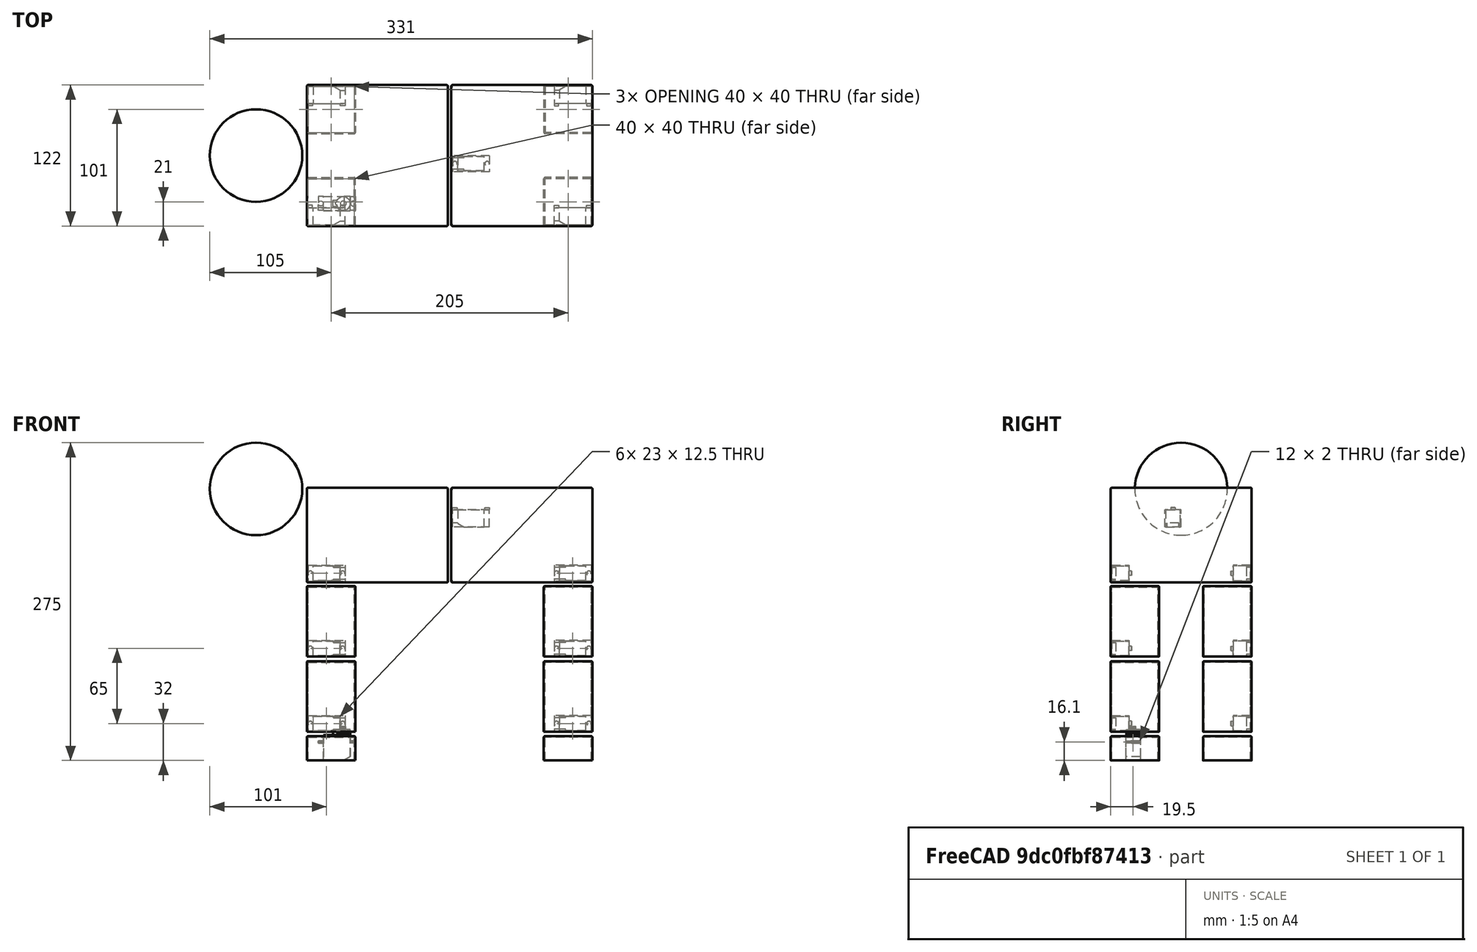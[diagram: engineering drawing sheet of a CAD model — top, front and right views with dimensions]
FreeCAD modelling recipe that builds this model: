
FCSTD DOCUMENT  (FreeCAD 0.21R33771 (Git))
Label: draft 1
License: All rights reserved
LicenseURL: https://en.wikipedia.org/wiki/All_rights_reserved
objects: Part::Box×42, Part::Cylinder×28, Part::Cut×28, Part::MultiFuse×18, Part::Feature×15, Part::Thickness×14, Part::Mirroring×3, Part::Sphere×1
note: 149 computed .brp shape members not serialized (recipe doc carries the construction recipe); baked Part::Feature solids carry a one-line shape summary decoded from their .brp

FEATURE [Part::Box] Box  label="leg down"
  AttacherType = Attacher::AttachEngine3D
  Height = 60
  Length = 40
  Placement = pos=(0,0,25) rot=(0,0,1;0rad)
  Width = 40
FEATURE [Part::Feature] _g_servo002_solid  label="9g_servo"
  Placement = pos=(25,18.5,11.1) rot=(0,0,1;0rad)
  shape: bbox 32 x 12.5 x 29.27 mm, 117 faces (baked)
FEATURE [Part::Box] Box001  label="paw"
  AttacherType = Attacher::AttachEngine3D
  Height = 20
  Length = 40
  Width = 40
FEATURE [Part::Box] Box003  label="Cube"
  AttacherType = Attacher::AttachEngine3D
  Height = 80
  Length = 120
  Placement = pos=(0,0,155) rot=(0,0,1;0rad)
  Width = 120
FEATURE [Part::Box] Box004  label="Cube001"
  AttacherType = Attacher::AttachEngine3D
  Height = 80
  Length = 120
  Placement = pos=(125,0,155) rot=(0,0,1;0rad)
  Width = 120
FEATURE [Part::Sphere] Sphere  label="Head"
  Angle1 = -90
  Angle2 = 90
  Angle3 = 360
  AttacherType = Attacher::AttachEngine3D
  Placement = pos=(-45,60,235) rot=(0,0,1;0rad)
  Radius = 40
FEATURE [Part::Box] Box015  label="Cube003"
  AttacherType = Attacher::AttachEngine3D
  Height = 14.9
  Length = 32
  Width = 14
FEATURE [Part::Box] Box016  label="Cube004"
  AttacherType = Attacher::AttachEngine3D
  Height = 3.5
  Length = 10
  Placement = pos=(22,2,0) rot=(0,0,1;0rad)
  Width = 10
FEATURE [Part::Cylinder] Cylinder002  label="Cylindre002"
  Angle = 360
  AttacherType = Attacher::AttachEngine3D
  FirstAngle = 0
  Height = 2.1
  Placement = pos=(2,7,14.9) rot=(0,0,1;0rad)
  Radius = 1.95
  SecondAngle = 0
FEATURE [Part::Cylinder] Cylinder003  label="Cylindre003"
  Angle = 360
  AttacherType = Attacher::AttachEngine3D
  FirstAngle = 0
  Height = 2.1
  Placement = pos=(30,7,14.9) rot=(0,0,1;0rad)
  Radius = 1.95
  SecondAngle = 0
FEATURE [Part::Feature] _g_servo002_solid002  label="9g_servo002"
  Placement = pos=(16,7,11) rot=(0,0,1;0rad)
  shape: bbox 32 x 12.5 x 29.27 mm, 117 faces (baked)
FEATURE [Part::Cut] Cut001
  Base = -> Box015
  Tool = -> _g_servo002_solid002
FEATURE [Part::MultiFuse] Fusion007
  Shapes = -> [Cut001,Cylinder002,Cylinder003]
FEATURE [Part::Cut] Cut002  label="ServoSocket"
  Base = -> Fusion007
  Placement = pos=(0,0,39) rot=(-1,0,0;1.5708rad)
  Tool = -> Box016
FEATURE [Part::Box] Box017  label="Cube005"
  AttacherType = Attacher::AttachEngine3D
  Height = 14.9
  Length = 32
  Width = 14
FEATURE [Part::Box] Box018  label="Cube006"
  AttacherType = Attacher::AttachEngine3D
  Height = 3.5
  Length = 10
  Placement = pos=(22,2,0) rot=(0,0,1;0rad)
  Width = 10
FEATURE [Part::Cylinder] Cylinder004  label="Cylindre004"
  Angle = 360
  AttacherType = Attacher::AttachEngine3D
  FirstAngle = 0
  Height = 2.1
  Placement = pos=(2,7,14.9) rot=(0,0,1;0rad)
  Radius = 1.95
  SecondAngle = 0
FEATURE [Part::Cylinder] Cylinder005  label="Cylindre005"
  Angle = 360
  AttacherType = Attacher::AttachEngine3D
  FirstAngle = 0
  Height = 2.1
  Placement = pos=(30,7,14.9) rot=(0,0,1;0rad)
  Radius = 1.95
  SecondAngle = 0
FEATURE [Part::Feature] _g_servo002_solid003  label="9g_servo003"
  Placement = pos=(16,7,11) rot=(0,0,1;0rad)
  shape: bbox 32 x 12.5 x 29.27 mm, 117 faces (baked)
FEATURE [Part::Cut] Cut003
  Base = -> Box017
  Tool = -> _g_servo002_solid003
FEATURE [Part::MultiFuse] Fusion008
  Shapes = -> [Cut003,Cylinder004,Cylinder005]
FEATURE [Part::Cut] Cut004  label="ServoSocket001"
  Base = -> Fusion008
  Placement = pos=(0,0,39) rot=(-1,0,0;1.5708rad)
  Tool = -> Box018
FEATURE [Part::Thickness] Thickness  label="LegDown"
  Faces = -> Box [Face5]
  Intersection = false
  Join = 0
  Mode = 0
  SelfIntersection = false
  Value = 1
FEATURE [Part::Thickness] Thickness002  label="Paw"
  Faces = -> Box001 [Face5]
  Intersection = false
  Join = 0
  Mode = 0
  SelfIntersection = false
  Value = 1
FEATURE [Part::Thickness] Thickness003  label="BodyFront"
  Faces = -> Box003
  Intersection = false
  Join = 0
  Mode = 0
  SelfIntersection = false
  Value = 1
FEATURE [Part::Thickness] Thickness004  label="BodyBack"
  Faces = -> Box004
  Intersection = false
  Join = 0
  Mode = 0
  SelfIntersection = false
  Value = 1
FEATURE [Part::Box] Box019  label="leg down001"
  AttacherType = Attacher::AttachEngine3D
  Height = 60
  Length = 40
  Placement = pos=(0,0,90) rot=(0,0,1;0rad)
  Width = 40
FEATURE [Part::Thickness] Thickness005  label="LegUp"
  Faces = -> Box019 [Face5]
  Intersection = false
  Join = 0
  Mode = 0
  SelfIntersection = false
  Value = 1
FEATURE [Part::Box] Box020  label="Cube007"
  AttacherType = Attacher::AttachEngine3D
  Height = 14.9
  Length = 32
  Width = 14
FEATURE [Part::Box] Box021  label="Cube008"
  AttacherType = Attacher::AttachEngine3D
  Height = 3.5
  Length = 10
  Placement = pos=(22,2,0) rot=(0,0,1;0rad)
  Width = 10
FEATURE [Part::Cylinder] Cylinder006  label="Cylindre006"
  Angle = 360
  AttacherType = Attacher::AttachEngine3D
  FirstAngle = 0
  Height = 2.1
  Placement = pos=(2,7,14.9) rot=(0,0,1;0rad)
  Radius = 1.95
  SecondAngle = 0
FEATURE [Part::Cylinder] Cylinder007  label="Cylindre007"
  Angle = 360
  AttacherType = Attacher::AttachEngine3D
  FirstAngle = 0
  Height = 2.1
  Placement = pos=(30,7,14.9) rot=(0,0,1;0rad)
  Radius = 1.95
  SecondAngle = 0
FEATURE [Part::Feature] _g_servo002_solid004  label="9g_servo004"
  Placement = pos=(16,7,11) rot=(0,0,1;0rad)
  shape: bbox 32 x 12.5 x 29.27 mm, 117 faces (baked)
FEATURE [Part::Cut] Cut005
  Base = -> Box020
  Tool = -> _g_servo002_solid004
FEATURE [Part::MultiFuse] Fusion009
  Shapes = -> [Cut005,Cylinder006,Cylinder007]
FEATURE [Part::Cut] Cut006  label="ServoSocket002"
  Base = -> Fusion009
  Placement = pos=(0,0,104) rot=(-1,0,0;1.5708rad)
  Tool = -> Box021
FEATURE [Part::Box] Box022  label="Cube009"
  AttacherType = Attacher::AttachEngine3D
  Height = 14.9
  Length = 32
  Width = 14
FEATURE [Part::Box] Box023  label="Cube010"
  AttacherType = Attacher::AttachEngine3D
  Height = 3.5
  Length = 10
  Placement = pos=(22,2,0) rot=(0,0,1;0rad)
  Width = 10
FEATURE [Part::Cylinder] Cylinder008  label="Cylindre008"
  Angle = 360
  AttacherType = Attacher::AttachEngine3D
  FirstAngle = 0
  Height = 2.1
  Placement = pos=(2,7,14.9) rot=(0,0,1;0rad)
  Radius = 1.95
  SecondAngle = 0
FEATURE [Part::Cylinder] Cylinder009  label="Cylindre009"
  Angle = 360
  AttacherType = Attacher::AttachEngine3D
  FirstAngle = 0
  Height = 2.1
  Placement = pos=(30,7,14.9) rot=(0,0,1;0rad)
  Radius = 1.95
  SecondAngle = 0
FEATURE [Part::Feature] _g_servo002_solid005  label="9g_servo005"
  Placement = pos=(16,7,11) rot=(0,0,1;0rad)
  shape: bbox 32 x 12.5 x 29.27 mm, 117 faces (baked)
FEATURE [Part::Cut] Cut007
  Base = -> Box022
  Tool = -> _g_servo002_solid005
FEATURE [Part::MultiFuse] Fusion010
  Shapes = -> [Cut007,Cylinder008,Cylinder009]
FEATURE [Part::Cut] Cut008  label="ServoSocket003"
  Base = -> Fusion010
  Placement = pos=(0,-1.4e-14,169) rot=(-1,0,0;1.5708rad)
  Tool = -> Box023
FEATURE [Part::Box] Box024  label="Cube011"
  AttacherType = Attacher::AttachEngine3D
  Height = 14.9
  Length = 32
  Width = 14
FEATURE [Part::Box] Box025  label="Cube012"
  AttacherType = Attacher::AttachEngine3D
  Height = 3.5
  Length = 10
  Placement = pos=(22,2,0) rot=(0,0,1;0rad)
  Width = 10
FEATURE [Part::Cylinder] Cylinder010  label="Cylindre010"
  Angle = 360
  AttacherType = Attacher::AttachEngine3D
  FirstAngle = 0
  Height = 2.1
  Placement = pos=(2,7,14.9) rot=(0,0,1;0rad)
  Radius = 1.95
  SecondAngle = 0
FEATURE [Part::Cylinder] Cylinder011  label="Cylindre011"
  Angle = 360
  AttacherType = Attacher::AttachEngine3D
  FirstAngle = 0
  Height = 2.1
  Placement = pos=(30,7,14.9) rot=(0,0,1;0rad)
  Radius = 1.95
  SecondAngle = 0
FEATURE [Part::Feature] _g_servo002_solid006  label="9g_servo006"
  Placement = pos=(16,7,11) rot=(0,0,1;0rad)
  shape: bbox 32 x 12.5 x 29.27 mm, 117 faces (baked)
FEATURE [Part::Cut] Cut009
  Base = -> Box024
  Tool = -> _g_servo002_solid006
FEATURE [Part::MultiFuse] Fusion011
  Shapes = -> [Cut009,Cylinder010,Cylinder011]
FEATURE [Part::Cut] Cut010  label="ServoSocket004"
  Base = -> Fusion011
  Placement = pos=(157,60,202) rot=(0,0,1;3.14159rad)
  Tool = -> Box025
FEATURE [Part::Box] Box026  label="leg down002"
  AttacherType = Attacher::AttachEngine3D
  Height = 60
  Length = 40
  Placement = pos=(0,0,25) rot=(0,0,1;0rad)
  Width = 40
FEATURE [Part::Box] Box027  label="paw001"
  AttacherType = Attacher::AttachEngine3D
  Height = 20
  Length = 40
  Width = 40
FEATURE [Part::Box] Box028  label="Cube013"
  AttacherType = Attacher::AttachEngine3D
  Height = 14.9
  Length = 32
  Width = 14
FEATURE [Part::Box] Box029  label="Cube014"
  AttacherType = Attacher::AttachEngine3D
  Height = 3.5
  Length = 10
  Placement = pos=(22,2,0) rot=(0,0,1;0rad)
  Width = 10
FEATURE [Part::Box] Box030  label="leg down003"
  AttacherType = Attacher::AttachEngine3D
  Height = 60
  Length = 40
  Placement = pos=(0,0,90) rot=(0,0,1;0rad)
  Width = 40
FEATURE [Part::Box] Box031  label="Cube015"
  AttacherType = Attacher::AttachEngine3D
  Height = 14.9
  Length = 32
  Width = 14
FEATURE [Part::Box] Box032  label="Cube016"
  AttacherType = Attacher::AttachEngine3D
  Height = 3.5
  Length = 10
  Placement = pos=(22,2,0) rot=(0,0,1;0rad)
  Width = 10
FEATURE [Part::Box] Box033  label="Cube017"
  AttacherType = Attacher::AttachEngine3D
  Height = 14.9
  Length = 32
  Width = 14
FEATURE [Part::Box] Box034  label="Cube018"
  AttacherType = Attacher::AttachEngine3D
  Height = 3.5
  Length = 10
  Placement = pos=(22,2,0) rot=(0,0,1;0rad)
  Width = 10
FEATURE [Part::Cylinder] Cylinder012  label="Cylindre012"
  Angle = 360
  AttacherType = Attacher::AttachEngine3D
  FirstAngle = 0
  Height = 2.1
  Placement = pos=(2,7,14.9) rot=(0,0,1;0rad)
  Radius = 1.95
  SecondAngle = 0
FEATURE [Part::Cylinder] Cylinder013  label="Cylindre013"
  Angle = 360
  AttacherType = Attacher::AttachEngine3D
  FirstAngle = 0
  Height = 2.1
  Placement = pos=(30,7,14.9) rot=(0,0,1;0rad)
  Radius = 1.95
  SecondAngle = 0
FEATURE [Part::Cylinder] Cylinder014  label="Cylindre014"
  Angle = 360
  AttacherType = Attacher::AttachEngine3D
  FirstAngle = 0
  Height = 2.1
  Placement = pos=(2,7,14.9) rot=(0,0,1;0rad)
  Radius = 1.95
  SecondAngle = 0
FEATURE [Part::Cylinder] Cylinder015  label="Cylindre015"
  Angle = 360
  AttacherType = Attacher::AttachEngine3D
  FirstAngle = 0
  Height = 2.1
  Placement = pos=(30,7,14.9) rot=(0,0,1;0rad)
  Radius = 1.95
  SecondAngle = 0
FEATURE [Part::Cylinder] Cylinder016  label="Cylindre016"
  Angle = 360
  AttacherType = Attacher::AttachEngine3D
  FirstAngle = 0
  Height = 2.1
  Placement = pos=(2,7,14.9) rot=(0,0,1;0rad)
  Radius = 1.95
  SecondAngle = 0
FEATURE [Part::Cylinder] Cylinder017  label="Cylindre017"
  Angle = 360
  AttacherType = Attacher::AttachEngine3D
  FirstAngle = 0
  Height = 2.1
  Placement = pos=(30,7,14.9) rot=(0,0,1;0rad)
  Radius = 1.95
  SecondAngle = 0
FEATURE [Part::Thickness] Thickness006  label="LegDown001"
  Faces = -> Box026 [Face5]
  Intersection = false
  Join = 0
  Mode = 0
  SelfIntersection = false
  Value = 1
FEATURE [Part::Thickness] Thickness007  label="Paw001"
  Faces = -> Box027 [Face5]
  Intersection = false
  Join = 0
  Mode = 0
  SelfIntersection = false
  Value = 1
FEATURE [Part::Thickness] Thickness008  label="LegUp001"
  Faces = -> Box030 [Face5]
  Intersection = false
  Join = 0
  Mode = 0
  SelfIntersection = false
  Value = 1
FEATURE [Part::Feature] _g_servo002_solid007  label="9g_servo007"
  Placement = pos=(16,7,11) rot=(0,0,1;0rad)
  shape: bbox 32 x 12.5 x 29.27 mm, 117 faces (baked)
FEATURE [Part::Cut] Cut011
  Base = -> Box028
  Tool = -> _g_servo002_solid007
FEATURE [Part::MultiFuse] Fusion013
  Shapes = -> [Cut011,Cylinder012,Cylinder013]
FEATURE [Part::Cut] Cut012  label="ServoSocket005"
  Base = -> Fusion013
  Placement = pos=(0,0,39) rot=(-1,0,0;1.5708rad)
  Tool = -> Box029
FEATURE [Part::Feature] _g_servo002_solid008  label="9g_servo008"
  Placement = pos=(16,7,11) rot=(0,0,1;0rad)
  shape: bbox 32 x 12.5 x 29.27 mm, 117 faces (baked)
FEATURE [Part::Cut] Cut013
  Base = -> Box031
  Tool = -> _g_servo002_solid008
FEATURE [Part::MultiFuse] Fusion014
  Shapes = -> [Cut013,Cylinder014,Cylinder015]
FEATURE [Part::Cut] Cut014  label="ServoSocket006"
  Base = -> Fusion014
  Placement = pos=(0,0,104) rot=(-1,0,0;1.5708rad)
  Tool = -> Box032
FEATURE [Part::Feature] _g_servo002_solid009  label="9g_servo009"
  Placement = pos=(16,7,11) rot=(0,0,1;0rad)
  shape: bbox 32 x 12.5 x 29.27 mm, 117 faces (baked)
FEATURE [Part::Cut] Cut015
  Base = -> Box033
  Tool = -> _g_servo002_solid009
FEATURE [Part::MultiFuse] Fusion015
  Shapes = -> [Cut015,Cylinder016,Cylinder017]
FEATURE [Part::Cut] Cut016  label="ServoSocket007"
  Base = -> Fusion015
  Placement = pos=(0,-1.4e-14,169) rot=(-1,0,0;1.5708rad)
  Tool = -> Box034
FEATURE [Part::MultiFuse] Fusion012
  Shapes = -> [Cut016,Cut012,Thickness006,Thickness007,Thickness008,Cut014]
FEATURE [Part::Mirroring] Part__Mirroring  label="Fusion012 (Mirror #1)"
  Base = (0,0,0)
  Normal = (0,1,0)
  Placement = pos=(0,120,0) rot=(0,0,1;0rad)
  Source = -> Fusion012
FEATURE [Part::Box] Box035  label="leg down004"
  AttacherType = Attacher::AttachEngine3D
  Height = 60
  Length = 40
  Placement = pos=(0,0,25) rot=(0,0,1;0rad)
  Width = 40
FEATURE [Part::Box] Box036  label="paw002"
  AttacherType = Attacher::AttachEngine3D
  Height = 20
  Length = 40
  Width = 40
FEATURE [Part::Box] Box037  label="Cube019"
  AttacherType = Attacher::AttachEngine3D
  Height = 14.9
  Length = 32
  Width = 14
FEATURE [Part::Box] Box038  label="Cube020"
  AttacherType = Attacher::AttachEngine3D
  Height = 3.5
  Length = 10
  Placement = pos=(22,2,0) rot=(0,0,1;0rad)
  Width = 10
FEATURE [Part::Box] Box039  label="leg down005"
  AttacherType = Attacher::AttachEngine3D
  Height = 60
  Length = 40
  Placement = pos=(0,0,90) rot=(0,0,1;0rad)
  Width = 40
FEATURE [Part::Box] Box040  label="Cube021"
  AttacherType = Attacher::AttachEngine3D
  Height = 14.9
  Length = 32
  Width = 14
FEATURE [Part::Box] Box041  label="Cube022"
  AttacherType = Attacher::AttachEngine3D
  Height = 3.5
  Length = 10
  Placement = pos=(22,2,0) rot=(0,0,1;0rad)
  Width = 10
FEATURE [Part::Box] Box042  label="Cube023"
  AttacherType = Attacher::AttachEngine3D
  Height = 14.9
  Length = 32
  Width = 14
FEATURE [Part::Box] Box043  label="Cube024"
  AttacherType = Attacher::AttachEngine3D
  Height = 3.5
  Length = 10
  Placement = pos=(22,2,0) rot=(0,0,1;0rad)
  Width = 10
FEATURE [Part::Box] Box044  label="leg down006"
  AttacherType = Attacher::AttachEngine3D
  Height = 60
  Length = 40
  Placement = pos=(0,0,25) rot=(0,0,1;0rad)
  Width = 40
FEATURE [Part::Box] Box045  label="paw003"
  AttacherType = Attacher::AttachEngine3D
  Height = 20
  Length = 40
  Width = 40
FEATURE [Part::Box] Box046  label="Cube025"
  AttacherType = Attacher::AttachEngine3D
  Height = 14.9
  Length = 32
  Width = 14
FEATURE [Part::Box] Box047  label="Cube026"
  AttacherType = Attacher::AttachEngine3D
  Height = 3.5
  Length = 10
  Placement = pos=(22,2,0) rot=(0,0,1;0rad)
  Width = 10
FEATURE [Part::Box] Box048  label="leg down007"
  AttacherType = Attacher::AttachEngine3D
  Height = 60
  Length = 40
  Placement = pos=(0,0,90) rot=(0,0,1;0rad)
  Width = 40
FEATURE [Part::Box] Box049  label="Cube027"
  AttacherType = Attacher::AttachEngine3D
  Height = 14.9
  Length = 32
  Width = 14
FEATURE [Part::Box] Box050  label="Cube028"
  AttacherType = Attacher::AttachEngine3D
  Height = 3.5
  Length = 10
  Placement = pos=(22,2,0) rot=(0,0,1;0rad)
  Width = 10
FEATURE [Part::Box] Box051  label="Cube029"
  AttacherType = Attacher::AttachEngine3D
  Height = 14.9
  Length = 32
  Width = 14
FEATURE [Part::Box] Box052  label="Cube030"
  AttacherType = Attacher::AttachEngine3D
  Height = 3.5
  Length = 10
  Placement = pos=(22,2,0) rot=(0,0,1;0rad)
  Width = 10
FEATURE [Part::Cylinder] Cylinder018  label="Cylindre018"
  Angle = 360
  AttacherType = Attacher::AttachEngine3D
  FirstAngle = 0
  Height = 2.1
  Placement = pos=(2,7,14.9) rot=(0,0,1;0rad)
  Radius = 1.95
  SecondAngle = 0
FEATURE [Part::Cylinder] Cylinder019  label="Cylindre019"
  Angle = 360
  AttacherType = Attacher::AttachEngine3D
  FirstAngle = 0
  Height = 2.1
  Placement = pos=(30,7,14.9) rot=(0,0,1;0rad)
  Radius = 1.95
  SecondAngle = 0
FEATURE [Part::Cylinder] Cylinder020  label="Cylindre020"
  Angle = 360
  AttacherType = Attacher::AttachEngine3D
  FirstAngle = 0
  Height = 2.1
  Placement = pos=(2,7,14.9) rot=(0,0,1;0rad)
  Radius = 1.95
  SecondAngle = 0
FEATURE [Part::Cylinder] Cylinder021  label="Cylindre021"
  Angle = 360
  AttacherType = Attacher::AttachEngine3D
  FirstAngle = 0
  Height = 2.1
  Placement = pos=(30,7,14.9) rot=(0,0,1;0rad)
  Radius = 1.95
  SecondAngle = 0
FEATURE [Part::Cylinder] Cylinder022  label="Cylindre022"
  Angle = 360
  AttacherType = Attacher::AttachEngine3D
  FirstAngle = 0
  Height = 2.1
  Placement = pos=(2,7,14.9) rot=(0,0,1;0rad)
  Radius = 1.95
  SecondAngle = 0
FEATURE [Part::Cylinder] Cylinder023  label="Cylindre023"
  Angle = 360
  AttacherType = Attacher::AttachEngine3D
  FirstAngle = 0
  Height = 2.1
  Placement = pos=(30,7,14.9) rot=(0,0,1;0rad)
  Radius = 1.95
  SecondAngle = 0
FEATURE [Part::Cylinder] Cylinder024  label="Cylindre024"
  Angle = 360
  AttacherType = Attacher::AttachEngine3D
  FirstAngle = 0
  Height = 2.1
  Placement = pos=(2,7,14.9) rot=(0,0,1;0rad)
  Radius = 1.95
  SecondAngle = 0
FEATURE [Part::Cylinder] Cylinder025  label="Cylindre025"
  Angle = 360
  AttacherType = Attacher::AttachEngine3D
  FirstAngle = 0
  Height = 2.1
  Placement = pos=(30,7,14.9) rot=(0,0,1;0rad)
  Radius = 1.95
  SecondAngle = 0
FEATURE [Part::Cylinder] Cylinder026  label="Cylindre026"
  Angle = 360
  AttacherType = Attacher::AttachEngine3D
  FirstAngle = 0
  Height = 2.1
  Placement = pos=(2,7,14.9) rot=(0,0,1;0rad)
  Radius = 1.95
  SecondAngle = 0
FEATURE [Part::Cylinder] Cylinder027  label="Cylindre027"
  Angle = 360
  AttacherType = Attacher::AttachEngine3D
  FirstAngle = 0
  Height = 2.1
  Placement = pos=(30,7,14.9) rot=(0,0,1;0rad)
  Radius = 1.95
  SecondAngle = 0
FEATURE [Part::Cylinder] Cylinder028  label="Cylindre028"
  Angle = 360
  AttacherType = Attacher::AttachEngine3D
  FirstAngle = 0
  Height = 2.1
  Placement = pos=(2,7,14.9) rot=(0,0,1;0rad)
  Radius = 1.95
  SecondAngle = 0
FEATURE [Part::Cylinder] Cylinder029  label="Cylindre029"
  Angle = 360
  AttacherType = Attacher::AttachEngine3D
  FirstAngle = 0
  Height = 2.1
  Placement = pos=(30,7,14.9) rot=(0,0,1;0rad)
  Radius = 1.95
  SecondAngle = 0
FEATURE [Part::Thickness] Thickness009  label="LegDown002"
  Faces = -> Box035 [Face5]
  Intersection = false
  Join = 0
  Mode = 0
  SelfIntersection = false
  Value = 1
FEATURE [Part::Thickness] Thickness010  label="Paw002"
  Faces = -> Box036 [Face5]
  Intersection = false
  Join = 0
  Mode = 0
  SelfIntersection = false
  Value = 1
FEATURE [Part::Thickness] Thickness011  label="LegUp002"
  Faces = -> Box039 [Face5]
  Intersection = false
  Join = 0
  Mode = 0
  SelfIntersection = false
  Value = 1
FEATURE [Part::Thickness] Thickness012  label="LegDown003"
  Faces = -> Box044 [Face5]
  Intersection = false
  Join = 0
  Mode = 0
  SelfIntersection = false
  Value = 1
FEATURE [Part::Thickness] Thickness013  label="Paw003"
  Faces = -> Box045 [Face5]
  Intersection = false
  Join = 0
  Mode = 0
  SelfIntersection = false
  Value = 1
FEATURE [Part::Thickness] Thickness014  label="LegUp003"
  Faces = -> Box048 [Face5]
  Intersection = false
  Join = 0
  Mode = 0
  SelfIntersection = false
  Value = 1
FEATURE [Part::Feature] _g_servo002_solid010  label="9g_servo010"
  Placement = pos=(16,7,11) rot=(0,0,1;0rad)
  shape: bbox 32 x 12.5 x 29.27 mm, 117 faces (baked)
FEATURE [Part::Cut] Cut017
  Base = -> Box037
  Tool = -> _g_servo002_solid010
FEATURE [Part::MultiFuse] Fusion018
  Shapes = -> [Cut017,Cylinder018,Cylinder019]
FEATURE [Part::Cut] Cut018  label="ServoSocket008"
  Base = -> Fusion018
  Placement = pos=(0,0,39) rot=(-1,0,0;1.5708rad)
  Tool = -> Box038
FEATURE [Part::Feature] _g_servo002_solid011  label="9g_servo011"
  Placement = pos=(16,7,11) rot=(0,0,1;0rad)
  shape: bbox 32 x 12.5 x 29.27 mm, 117 faces (baked)
FEATURE [Part::Cut] Cut019
  Base = -> Box040
  Tool = -> _g_servo002_solid011
FEATURE [Part::MultiFuse] Fusion019
  Shapes = -> [Cut019,Cylinder020,Cylinder021]
FEATURE [Part::Cut] Cut020  label="ServoSocket009"
  Base = -> Fusion019
  Placement = pos=(0,0,104) rot=(-1,0,0;1.5708rad)
  Tool = -> Box041
FEATURE [Part::Feature] _g_servo002_solid012  label="9g_servo012"
  Placement = pos=(16,7,11) rot=(0,0,1;0rad)
  shape: bbox 32 x 12.5 x 29.27 mm, 117 faces (baked)
FEATURE [Part::Cut] Cut021
  Base = -> Box042
  Tool = -> _g_servo002_solid012
FEATURE [Part::MultiFuse] Fusion020
  Shapes = -> [Cut021,Cylinder022,Cylinder023]
FEATURE [Part::Cut] Cut022  label="ServoSocket010"
  Base = -> Fusion020
  Placement = pos=(0,-1.4e-14,169) rot=(-1,0,0;1.5708rad)
  Tool = -> Box043
FEATURE [Part::MultiFuse] Fusion017
  Shapes = -> [Cut022,Cut018,Thickness009,Thickness010,Thickness011,Cut020]
FEATURE [Part::Feature] _g_servo002_solid013  label="9g_servo013"
  Placement = pos=(16,7,11) rot=(0,0,1;0rad)
  shape: bbox 32 x 12.5 x 29.27 mm, 117 faces (baked)
FEATURE [Part::Cut] Cut023
  Base = -> Box046
  Tool = -> _g_servo002_solid013
FEATURE [Part::MultiFuse] Fusion022
  Shapes = -> [Cut023,Cylinder024,Cylinder025]
FEATURE [Part::Cut] Cut024  label="ServoSocket011"
  Base = -> Fusion022
  Placement = pos=(0,0,39) rot=(-1,0,0;1.5708rad)
  Tool = -> Box047
FEATURE [Part::Feature] _g_servo002_solid014  label="9g_servo014"
  Placement = pos=(16,7,11) rot=(0,0,1;0rad)
  shape: bbox 32 x 12.5 x 29.27 mm, 117 faces (baked)
FEATURE [Part::Cut] Cut025
  Base = -> Box049
  Tool = -> _g_servo002_solid014
FEATURE [Part::MultiFuse] Fusion023
  Shapes = -> [Cut025,Cylinder026,Cylinder027]
FEATURE [Part::Cut] Cut026  label="ServoSocket012"
  Base = -> Fusion023
  Placement = pos=(0,0,104) rot=(-1,0,0;1.5708rad)
  Tool = -> Box050
FEATURE [Part::Feature] _g_servo002_solid015  label="9g_servo015"
  Placement = pos=(16,7,11) rot=(0,0,1;0rad)
  shape: bbox 32 x 12.5 x 29.27 mm, 117 faces (baked)
FEATURE [Part::Cut] Cut027
  Base = -> Box051
  Tool = -> _g_servo002_solid015
FEATURE [Part::MultiFuse] Fusion024
  Shapes = -> [Cut027,Cylinder028,Cylinder029]
FEATURE [Part::Cut] Cut028  label="ServoSocket013"
  Base = -> Fusion024
  Placement = pos=(0,-1.4e-14,169) rot=(-1,0,0;1.5708rad)
  Tool = -> Box052
FEATURE [Part::MultiFuse] Fusion021
  Shapes = -> [Cut028,Cut024,Thickness012,Thickness013,Thickness014,Cut026]
FEATURE [Part::Mirroring] Part__Mirroring001  label="Fusion012 (Mirror #1)001"
  Base = (0,0,0)
  Normal = (0,1,0)
  Placement = pos=(0,120,0) rot=(0,0,1;0rad)
  Source = -> Fusion021
FEATURE [Part::MultiFuse] Fusion025
  Shapes = -> [Fusion017,Part__Mirroring001]
FEATURE [Part::Mirroring] Part__Mirroring002  label="Fusion025 (Mirror #3)"
  Base = (0,0,0)
  Normal = (1,0,0)
  Placement = pos=(245,0,0) rot=(0,0,1;0rad)
  Source = -> Fusion025
